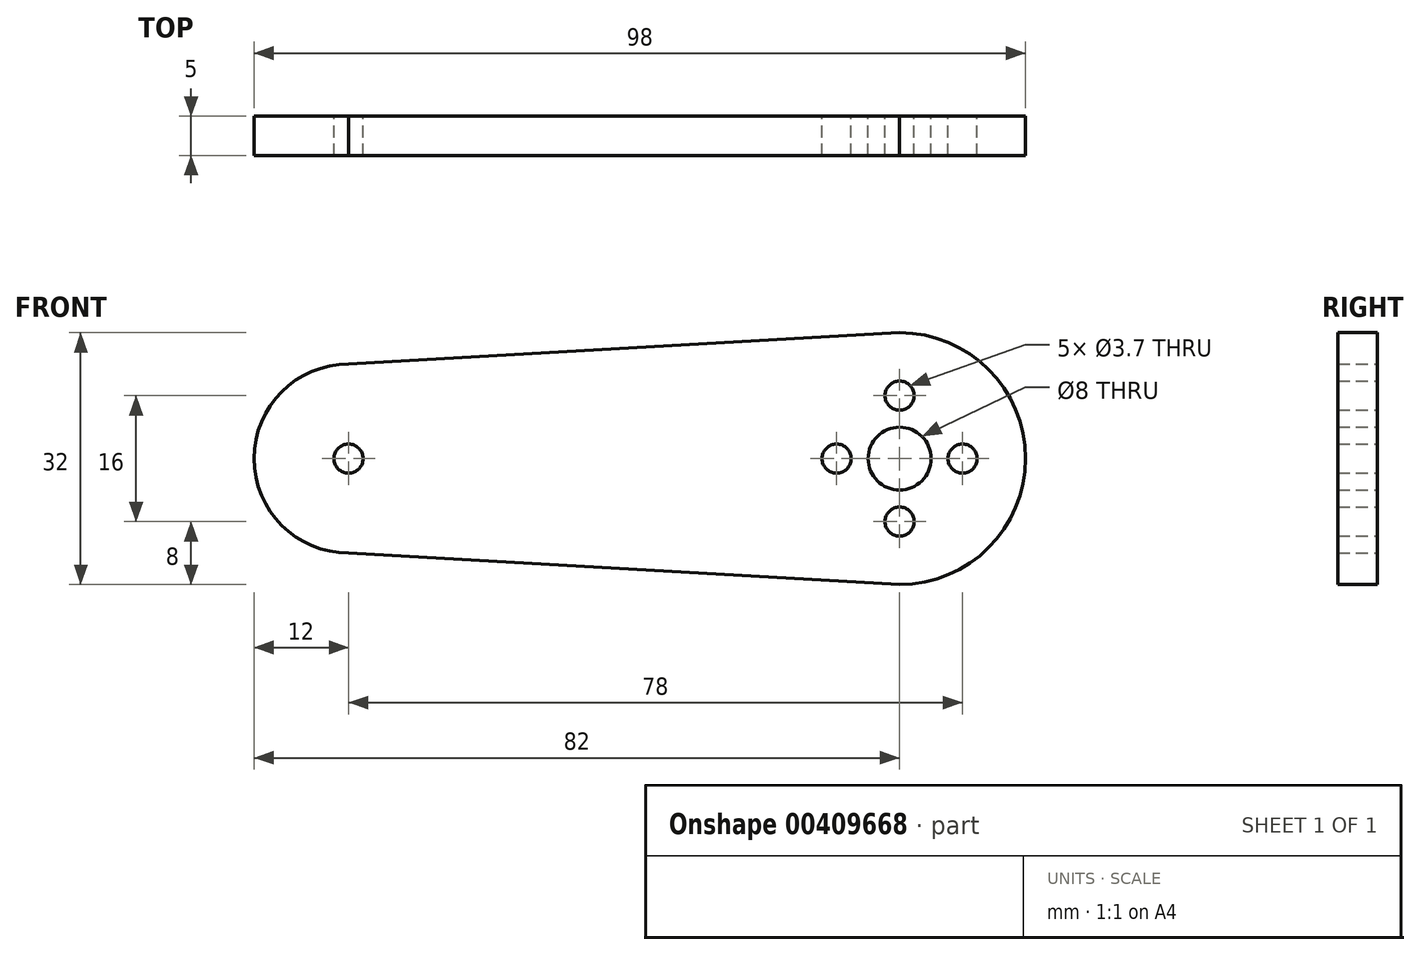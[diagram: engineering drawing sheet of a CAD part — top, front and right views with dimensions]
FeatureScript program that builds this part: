
annotation { "Feature Type Name" : "Feature", "Feature Type Description" : "" }
export const myFeature = defineFeature(function(context is Context, id is Id, definition is map)
    precondition{}
    {
        {
            var Q0;
            Q0=qCreatedBy(makeId("Front.planeOp"),FACE);
            var sketch = newSketch(context, id + "F0", { "sketchPlane" : qUnion([Q0])});
            skCircle(sketch, "E0", {"center": v(-35, 0) * mm, "radius": 1.85 * mm});
            skCircle(sketch, "E1", {"center": v(35, 0) * mm, "radius": 4 * mm});
            skCircle(sketch, "E2", {"center": v(35, 8) * mm, "radius": 1.85 * mm});
            skCircle(sketch, "E3.1.0", {"center": v(27, 0) * mm, "radius": 1.85 * mm});
            skCircle(sketch, "E3.2.0", {"center": v(35, -8) * mm, "radius": 1.85 * mm});
            skCircle(sketch, "E3.3.0", {"center": v(43, 0) * mm, "radius": 1.85 * mm});
            skArc(sketch, "E4", {"start": v(-35, -12) * mm, "mid": v(-47, 0) * mm, "end": v(-35, 12) * mm});
            skArc(sketch, "E5", {"start": v(35, -16) * mm, "mid": v(51, 0) * mm, "end": v(35, 16) * mm});
            skLineSegment(sketch, "E6", {"start": v(-35, 12) * mm, "end": v(35, 16) * mm});
            skLineSegment(sketch, "E7", {"start": v(35, -16) * mm, "end": v(-35, -12) * mm});
            skSolve(sketch);
        }
        {
            var Q0;
            Q0=makeQuery(id+"F0.imprint","IMPRINT",FACE,{"disambiguationData":[TD([[makeQuery(id+"F0.imprint","IMPRINT",EDGE,{"derivedFrom":sQuery(id+"F0.wireOp",EDGE,"E0")}),-1.0]])]});
            extrude(context, id + "F1", {"entities" : qUnion([Q0]), "endBound" : BoundingType.SYMMETRIC, "depth" : 5 * mm});
        }
    });
